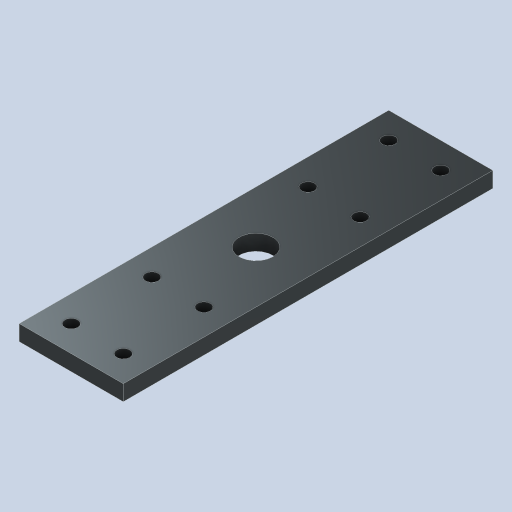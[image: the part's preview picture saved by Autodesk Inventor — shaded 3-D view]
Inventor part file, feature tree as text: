
AUTODESK INVENTOR PART (.ipt)
format: ipt  version: 2023 (Build 270158000, 158)  size: 143,872 bytes
history: native  units: mm
features: sketch x3, hole x2, other x1, extrude x1
ambient origin geometry x8: Origin, YZ Plane, XZ Plane, XY Plane, X Axis, Y Axis, Z Axis, Center Point
bodies: Body1 (feature_tree)
feature tree (7):
  other  "Sólido1"
  extrude  "Extrusão1"  Depth=142.0mm
  hole  "Furo1"  [1 undecoded]
  hole  "Furo3"  [1 undecoded]
  sketch  "Esboço1"  dims[d0=40.0mm d1=142.0mm]
  sketch  "Esboço2"  dims[d2=6.0mm d3=0.0mm d4=142.0mm]
  sketch  "Esboço4"  dims[d5=40.0mm d6=20.0mm d7=71.0mm d8=13.0mm d9=6.0mm d10=4.0mm d11=2.0mm d12=90.0deg d13=0.5mm d14=20.594885mm d19=40.0mm d20=10.0mm d21=10.0mm d45=40.0mm d46=10.0mm d47=10.0mm d48=10.0mm d49=10.0mm d50=5.0mm d51=6.0mm d52=3.023mm d53=2.0mm d54=14.3117mm d55=0.5mm d56=20.594885mm d57=10.0mm d58=10.0mm d59=10.0mm d60=60.0mm d61=30.0mm]
note: 2 required parameter values undecoded (feature->parameter linkage not recoverable at this tier; creation-order binding heuristic only, values carry confidence <= 0.55)
